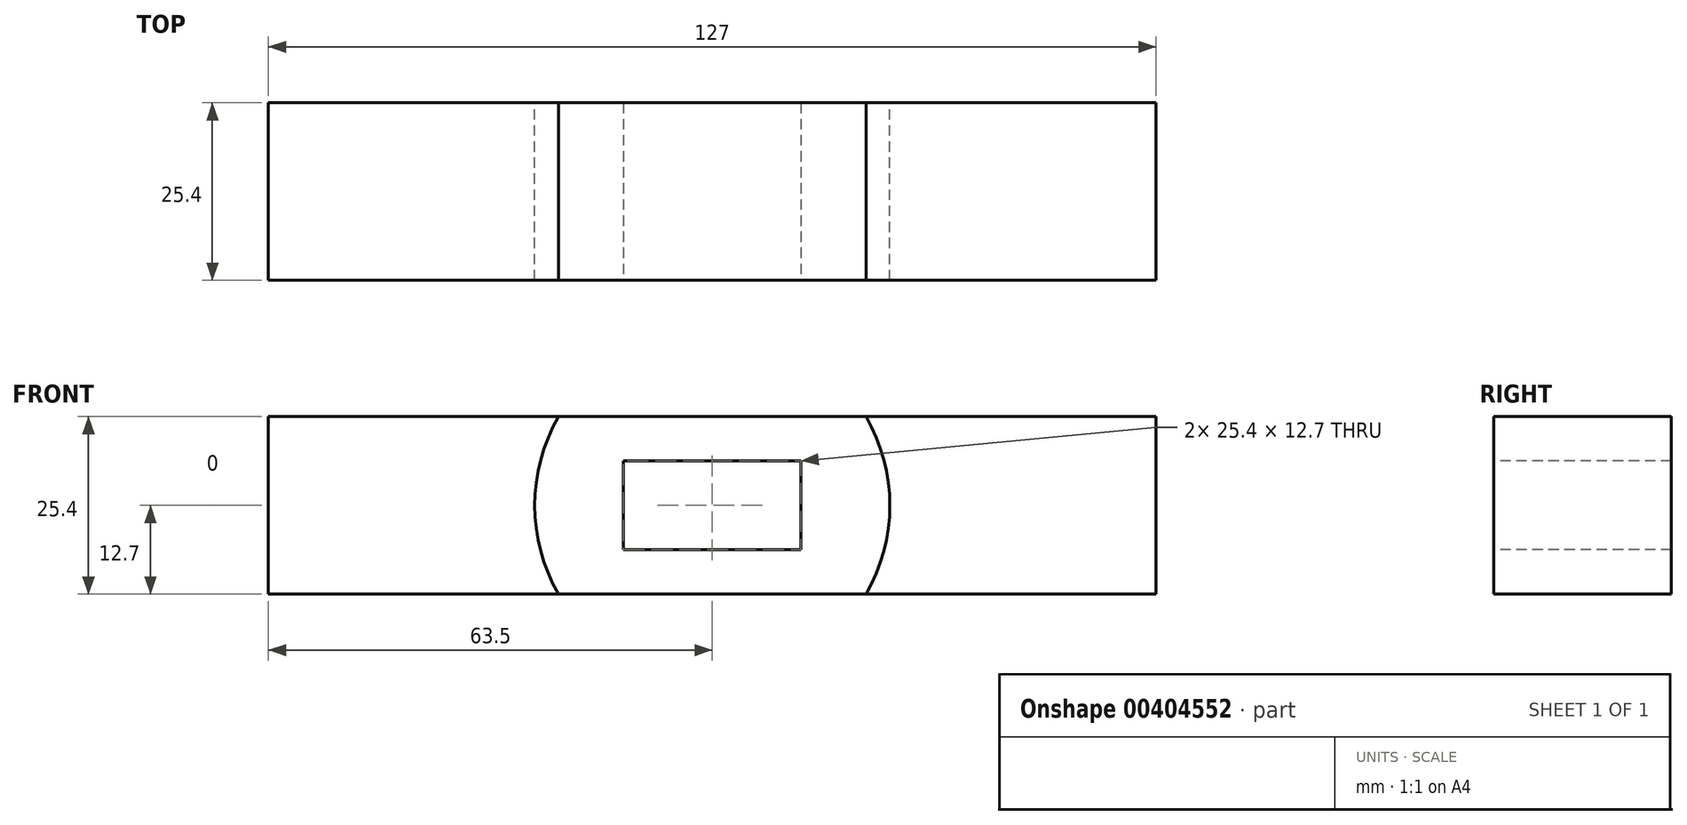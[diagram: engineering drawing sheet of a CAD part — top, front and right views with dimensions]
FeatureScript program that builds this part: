
annotation { "Feature Type Name" : "Feature", "Feature Type Description" : "" }
export const myFeature = defineFeature(function(context is Context, id is Id, definition is map)
    precondition{}
    {
        {
            var Q0;
            Q0=qCreatedBy(makeId("Front.planeOp"),FACE);
            var sketch = newSketch(context, id + "F0", { "sketchPlane" : qUnion([Q0])});
            skLineSegment(sketch, "E0.bottom", {"start": v(63.5, -12.7) * mm, "end": v(-63.5, -12.7) * mm});
            skLineSegment(sketch, "E0.top", {"start": v(63.5, 12.7) * mm, "end": v(-63.5, 12.7) * mm});
            skLineSegment(sketch, "E0.left", {"start": v(63.5, -12.7) * mm, "end": v(63.5, 12.7) * mm});
            skLineSegment(sketch, "E0.right", {"start": v(-63.5, -12.7) * mm, "end": v(-63.5, 12.7) * mm});
            skPoint(sketch, "E0.middle", {"position": v(0, 0) * mm});
            skSolve(sketch);
        }
        {
            var Q0;
            Q0=makeQuery(id+"F0.imprint","IMPRINT",FACE,{"disambiguationData":[TD([[makeQuery(id+"F0.imprint","IMPRINT",EDGE,{"derivedFrom":sQuery(id+"F0.wireOp",EDGE,"E0.bottom")}),-1.0]])]});
            var sketch = newSketch(context, id + "F1", { "sketchPlane" : qUnion([Q0])});
            skCircle(sketch, "E1", {"center": v(0, 0) * mm, "radius": 25.4 * mm});
            skSolve(sketch);
        }
        {
            var Q0;
            Q0=makeQuery(id+"F0.imprint","IMPRINT",FACE,{"disambiguationData":[TD([[makeQuery(id+"F0.imprint","IMPRINT",EDGE,{"derivedFrom":sQuery(id+"F0.wireOp",EDGE,"E0.bottom")}),-1.0]])]});
            var Q1;
            {var subQ0=sQuery(id+"F1.wireOp",EDGE,"E1");var subQ1=makeQuery(id+"F0.imprint","IMPRINT",EDGE,{"derivedFrom":sQuery(id+"F0.wireOp",EDGE,"E0.top")});var subQ2=makeQuery(id+"F1.imprint","INTERSECT",VERTEX,{"disambiguationData":[OD(0.0)],"derivedFrom":[subQ1,subQ0]});Q1=makeQuery(id+"F1.imprint","IMPRINT",FACE,{"disambiguationData":[TD([[makeQuery(id+"F1.imprint","IMPRINT",EDGE,{"disambiguationData":[TD([[subQ2,1.0]])],"derivedFrom":subQ0}),1.0]])]});}
            var Q2;
            {var subQ0=sQuery(id+"F1.wireOp",EDGE,"E1");var subQ1=makeQuery(id+"F0.imprint","IMPRINT",EDGE,{"derivedFrom":sQuery(id+"F0.wireOp",EDGE,"E0.bottom")});var subQ2=makeQuery(id+"F1.imprint","INTERSECT",VERTEX,{"disambiguationData":[OD(0.0)],"derivedFrom":[subQ1,subQ0]});Q2=makeQuery(id+"F1.imprint","IMPRINT",FACE,{"disambiguationData":[TD([[makeQuery(id+"F1.imprint","IMPRINT",EDGE,{"disambiguationData":[TD([[subQ2,-1.0]])],"derivedFrom":subQ0}),1.0]])]});}
            extrude(context, id + "F2", {"entities" : qUnion([Q0, Q1, Q2]), "depth" : 25.4 * mm});
        }
        {
            var Q0;
            Q0=makeQuery(id+"F2.opExtrude","CAP_FACE",FACE,{"disambiguationData":[OSD([sQuery(id+"F0.wireOp",EDGE,"E0.bottom"),sQuery(id+"F0.wireOp",EDGE,"E0.top"),sQuery(id+"F0.wireOp",EDGE,"E0.left"),sQuery(id+"F0.wireOp",EDGE,"E0.right")])],"isStart":false});
            var sketch = newSketch(context, id + "F3", { "sketchPlane" : qUnion([Q0])});
            skLineSegment(sketch, "E2.bottom", {"start": v(12.7, -6.35) * mm, "end": v(-12.7, -6.35) * mm});
            skLineSegment(sketch, "E2.top", {"start": v(12.7, 6.35) * mm, "end": v(-12.7, 6.35) * mm});
            skLineSegment(sketch, "E2.left", {"start": v(12.7, -6.35) * mm, "end": v(12.7, 6.35) * mm});
            skLineSegment(sketch, "E2.right", {"start": v(-12.7, -6.35) * mm, "end": v(-12.7, 6.35) * mm});
            skPoint(sketch, "E2.middle", {"position": v(0, 0) * mm});
            skSolve(sketch);
        }
        {
            var Q0;
            Q0=qSketchRegion(id+"F3",true);
            extrude(context, id + "F4", {"entities" : qUnion([Q0]), "operationType" : NewBodyOperationType.REMOVE, "oppositeDirection" : true, "depth" : 25.4 * mm});
        }
    });
